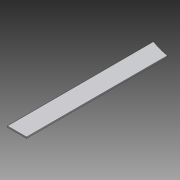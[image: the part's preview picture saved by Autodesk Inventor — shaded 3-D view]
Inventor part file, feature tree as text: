
AUTODESK INVENTOR PART (.ipt)
format: ipt  version: 2014 SP1 (Build 180222100, 222)  size: 75,264 bytes
history: native  units: in
note: dims shown in document units (in); Inventor stores cm internally (conversion verified against a paired STEP export)
features: extrude x1, sketch x1
ambient origin geometry x8: Origin, YZ Plane, XZ Plane, XY Plane, X Axis, Y Axis, Z Axis, Center Point
bodies: Solid1 (feature_tree)
feature tree (2):
  extrude  "Extrusion1"  Depth=0.0625in
  sketch  "Sketch1"  dims[d0=11.5in d1=13.0in d2=13.0in d5=1.0in d9=6.75in d11=0.0625in d12=0.0in]
